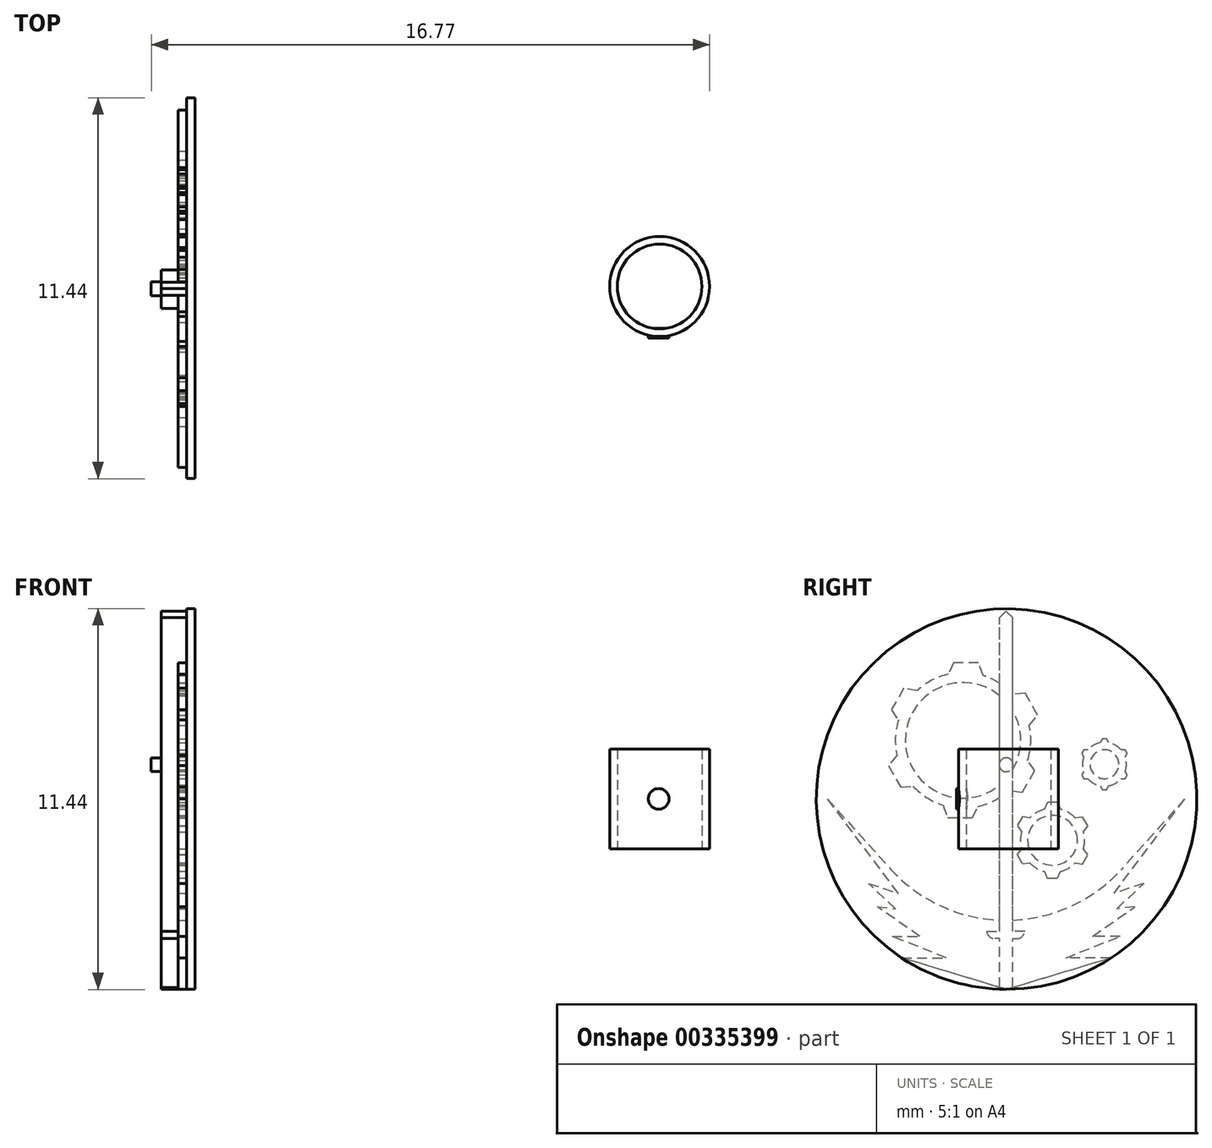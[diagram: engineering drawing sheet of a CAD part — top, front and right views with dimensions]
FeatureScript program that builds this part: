
annotation { "Feature Type Name" : "Feature", "Feature Type Description" : "" }
export const myFeature = defineFeature(function(context is Context, id is Id, definition is map)
    precondition{}
    {
        {
            var Q0;
            Q0=qCreatedBy(makeId("Right.planeOp"),FACE);
            var sketch = newSketch(context, id + "F0", { "sketchPlane" : qUnion([Q0])});
            skCircle(sketch, "E0", {"center": v(0, 0) * mm, "radius": 5.53 * mm});
            skCircle(sketch, "E1", {"center": v(0, 0) * mm, "radius": 5.72 * mm});
            skSolve(sketch);
        }
        {
            var Q0;
            Q0 = qSketchRegion(id + "F0", true);
            var Q1;
            Q1=makeQuery(id+"F0.imprint","IMPRINT",FACE,{"disambiguationData":[TD([[makeQuery(id+"F0.imprint","IMPRINT",EDGE,{"derivedFrom":sQuery(id+"F0.wireOp",EDGE,"E0")}),1.0]])]});
            extrude(context, id + "F1", {"entities" : qUnion([Q0, Q1]), "depth" : 0.25 * mm});
        }
        {
            var Q0;
            Q0=makeQuery(id+"F1.opExtrude","CAP_FACE",FACE,{"disambiguationData":[OSD([sQuery(id+"F0.wireOp",EDGE,"E1")])],"isStart":true});
            var sketch = newSketch(context, id + "F2", { "sketchPlane" : qUnion([Q0])});
            skLineSegment(sketch, "E2", {"start": v(-0.18, -6.05) * mm, "end": v(0.2, -6.05) * mm});
            skLineSegment(sketch, "E3", {"start": v(0.2, -6.05) * mm, "end": v(0.2, -4.2) * mm});
            skLineSegment(sketch, "E4", {"start": v(-0.18, -6.05) * mm, "end": v(-0.18, -4.2) * mm});
            skLineSegment(sketch, "E5", {"start": v(-0.18, -4.2) * mm, "end": v(-0.55, -4.2) * mm});
            skLineSegment(sketch, "E6", {"start": v(-0.55, -4.2) * mm, "end": v(-0.55, -3.97) * mm});
            skLineSegment(sketch, "E7", {"start": v(0.2, -4.2) * mm, "end": v(0.6, -4.2) * mm});
            skLineSegment(sketch, "E8", {"start": v(0.6, -4.2) * mm, "end": v(0.6, -3.97) * mm});
            skLineSegment(sketch, "E9", {"start": v(0.6, -3.97) * mm, "end": v(0.2, -3.97) * mm});
            skLineSegment(sketch, "E10", {"start": v(-0.55, -3.97) * mm, "end": v(-0.18, -3.97) * mm});
            skLineSegment(sketch, "E11", {"start": v(-0.18, -3.97) * mm, "end": v(-0.18, 6.04) * mm});
            skLineSegment(sketch, "E12", {"start": v(0.2, -3.97) * mm, "end": v(0.2, 6.04) * mm});
            skLineSegment(sketch, "E13", {"start": v(-0.18, 6.04) * mm, "end": v(0.2, 6.04) * mm});
            skCircle(sketch, "E14", {"center": v(-1.38, -1.24) * mm, "radius": 0.96 * mm});
            skCircle(sketch, "E15", {"center": v(-1.38, -1.24) * mm, "radius": 0.75 * mm});
            skCircle(sketch, "E16", {"center": v(-2.94, 1.05) * mm, "radius": 0.66 * mm});
            skCircle(sketch, "E17", {"center": v(-2.94, 1.05) * mm, "radius": 0.43 * mm});
            skCircle(sketch, "E18", {"center": v(1.3, 1.76) * mm, "radius": 2.04 * mm});
            skCircle(sketch, "E19", {"center": v(1.3, 1.76) * mm, "radius": 1.73 * mm});
            skLineSegment(sketch, "E20", {"start": v(0.2, 1.03) * mm, "end": v(-0.18, 1.03) * mm, "construction": true});
            skCircle(sketch, "E21", {"center": v(0.01, 1.03) * mm, "radius": 4.67 * mm});
            skLineSegment(sketch, "E22", {"start": v(0.01, -5.71) * mm, "end": v(3.15, -4.77) * mm});
            skPoint(sketch, "E22.startSnap0", {"position": v(0.01, -6.05) * mm});
            skLineSegment(sketch, "E23", {"start": v(3.15, -4.77) * mm, "end": v(1.8, -4.77) * mm});
            skLineSegment(sketch, "E24", {"start": v(1.8, -4.77) * mm, "end": v(3.44, -4.12) * mm});
            skLineSegment(sketch, "E25", {"start": v(3.44, -4.12) * mm, "end": v(2.6, -4.12) * mm});
            skLineSegment(sketch, "E26", {"start": v(2.6, -4.12) * mm, "end": v(3.88, -3.23) * mm});
            skLineSegment(sketch, "E27", {"start": v(3.88, -3.23) * mm, "end": v(3.34, -3.3) * mm});
            skLineSegment(sketch, "E28", {"start": v(3.34, -3.3) * mm, "end": v(4.15, -2.54) * mm});
            skLineSegment(sketch, "E29", {"start": v(4.15, -2.54) * mm, "end": v(3.25, -2.83) * mm});
            skLineSegment(sketch, "E30", {"start": v(3.25, -2.83) * mm, "end": v(5.38, 0) * mm});
            skLineSegment(sketch, "E31", {"start": v(5.38, 0) * mm, "end": v(2.83, -2.83) * mm});
            skLineSegment(sketch, "E32", {"start": v(0.01, 6.04) * mm, "end": v(0.01, -6.05) * mm, "construction": true});
            skLineSegment(sketch, "E33.MirrorCS", {"start": v(0.01, -5.71) * mm, "end": v(-3.12, -4.77) * mm});
            skLineSegment(sketch, "E34.MirrorCS", {"start": v(-3.12, -4.77) * mm, "end": v(-1.78, -4.77) * mm});
            skLineSegment(sketch, "E35.MirrorCS", {"start": v(-1.78, -4.77) * mm, "end": v(-3.41, -4.12) * mm});
            skLineSegment(sketch, "E36.MirrorCS", {"start": v(-3.41, -4.12) * mm, "end": v(-2.58, -4.12) * mm});
            skLineSegment(sketch, "E37.MirrorCS", {"start": v(-2.58, -4.12) * mm, "end": v(-3.86, -3.23) * mm});
            skLineSegment(sketch, "E38.MirrorCS", {"start": v(-3.86, -3.23) * mm, "end": v(-3.31, -3.3) * mm});
            skLineSegment(sketch, "E39.MirrorCS", {"start": v(-3.31, -3.3) * mm, "end": v(-4.12, -2.54) * mm});
            skLineSegment(sketch, "E40.MirrorCS", {"start": v(-4.12, -2.54) * mm, "end": v(-3.23, -2.83) * mm});
            skLineSegment(sketch, "E41.MirrorCS", {"start": v(-3.23, -2.83) * mm, "end": v(-5.35, 0) * mm});
            skLineSegment(sketch, "E42.MirrorCS", {"start": v(-5.35, 0) * mm, "end": v(-2.8, -2.83) * mm});
            skLineSegment(sketch, "E43", {"start": v(-3.07, 1.7) * mm, "end": v(-3, 1.8) * mm});
            skLineSegment(sketch, "E44", {"start": v(-3, 1.8) * mm, "end": v(-2.88, 1.8) * mm});
            skLineSegment(sketch, "E45", {"start": v(-2.88, 1.8) * mm, "end": v(-2.81, 1.7) * mm});
            skLineSegment(sketch, "E46.1.0", {"start": v(-3.56, 1.48) * mm, "end": v(-3.44, 1.48) * mm});
            skLineSegment(sketch, "E46.1.1", {"start": v(-3.63, 1.37) * mm, "end": v(-3.56, 1.48) * mm});
            skLineSegment(sketch, "E46.1.2", {"start": v(-3.56, 1.26) * mm, "end": v(-3.63, 1.37) * mm});
            skLineSegment(sketch, "E46.2.0", {"start": v(-3.63, 0.72) * mm, "end": v(-3.56, 0.83) * mm});
            skLineSegment(sketch, "E46.2.1", {"start": v(-3.56, 0.61) * mm, "end": v(-3.63, 0.72) * mm});
            skLineSegment(sketch, "E46.2.2", {"start": v(-3.44, 0.61) * mm, "end": v(-3.56, 0.61) * mm});
            skLineSegment(sketch, "E46.3.0", {"start": v(-3, 0.29) * mm, "end": v(-3.07, 0.4) * mm});
            skLineSegment(sketch, "E46.3.1", {"start": v(-2.88, 0.29) * mm, "end": v(-3, 0.29) * mm});
            skLineSegment(sketch, "E46.3.2", {"start": v(-2.81, 0.4) * mm, "end": v(-2.88, 0.29) * mm});
            skLineSegment(sketch, "E46.4.0", {"start": v(-2.32, 0.61) * mm, "end": v(-2.44, 0.61) * mm});
            skLineSegment(sketch, "E46.4.1", {"start": v(-2.25, 0.72) * mm, "end": v(-2.32, 0.61) * mm});
            skLineSegment(sketch, "E46.4.2", {"start": v(-2.32, 0.83) * mm, "end": v(-2.25, 0.72) * mm});
            skLineSegment(sketch, "E46.5.0", {"start": v(-2.25, 1.37) * mm, "end": v(-2.32, 1.26) * mm});
            skLineSegment(sketch, "E46.5.1", {"start": v(-2.32, 1.48) * mm, "end": v(-2.25, 1.37) * mm});
            skLineSegment(sketch, "E46.5.2", {"start": v(-2.44, 1.48) * mm, "end": v(-2.32, 1.48) * mm});
            skLineSegment(sketch, "E47", {"start": v(-1.62, -0.3) * mm, "end": v(-1.54, -0.1) * mm});
            skLineSegment(sketch, "E48", {"start": v(-1.54, -0.1) * mm, "end": v(-1.23, -0.1) * mm});
            skLineSegment(sketch, "E49", {"start": v(-1.23, -0.1) * mm, "end": v(-1.14, -0.3) * mm});
            skLineSegment(sketch, "E50.1.0", {"start": v(-2.3, -0.98) * mm, "end": v(-2.45, -0.81) * mm});
            skLineSegment(sketch, "E50.1.1", {"start": v(-2.45, -0.81) * mm, "end": v(-2.29, -0.54) * mm});
            skLineSegment(sketch, "E50.1.2", {"start": v(-2.29, -0.54) * mm, "end": v(-2.06, -0.56) * mm});
            skLineSegment(sketch, "E50.2.0", {"start": v(-2.06, -1.92) * mm, "end": v(-2.28, -1.95) * mm});
            skLineSegment(sketch, "E50.2.1", {"start": v(-2.28, -1.95) * mm, "end": v(-2.44, -1.68) * mm});
            skLineSegment(sketch, "E50.2.2", {"start": v(-2.44, -1.68) * mm, "end": v(-2.3, -1.5) * mm});
            skLineSegment(sketch, "E50.3.0", {"start": v(-1.14, -2.17) * mm, "end": v(-1.22, -2.38) * mm});
            skLineSegment(sketch, "E50.3.1", {"start": v(-1.22, -2.38) * mm, "end": v(-1.53, -2.38) * mm});
            skLineSegment(sketch, "E50.3.2", {"start": v(-1.53, -2.38) * mm, "end": v(-1.62, -2.17) * mm});
            skLineSegment(sketch, "E50.4.0", {"start": v(-0.45, -1.5) * mm, "end": v(-0.31, -1.67) * mm});
            skLineSegment(sketch, "E50.4.1", {"start": v(-0.31, -1.67) * mm, "end": v(-0.47, -1.94) * mm});
            skLineSegment(sketch, "E50.4.2", {"start": v(-0.47, -1.94) * mm, "end": v(-0.7, -1.92) * mm});
            skLineSegment(sketch, "E50.5.0", {"start": v(-0.7, -0.56) * mm, "end": v(-0.48, -0.53) * mm});
            skLineSegment(sketch, "E50.5.1", {"start": v(-0.48, -0.53) * mm, "end": v(-0.32, -0.8) * mm});
            skLineSegment(sketch, "E50.5.2", {"start": v(-0.32, -0.8) * mm, "end": v(-0.45, -0.98) * mm});
            skLineSegment(sketch, "E51", {"start": v(0.7, 3.7) * mm, "end": v(0.84, 4.09) * mm});
            skLineSegment(sketch, "E52", {"start": v(0.84, 4.09) * mm, "end": v(1.6, 4.09) * mm});
            skLineSegment(sketch, "E53", {"start": v(1.6, 4.09) * mm, "end": v(1.75, 3.75) * mm});
            skLineSegment(sketch, "E54.1.0", {"start": v(-0.68, 2.21) * mm, "end": v(-0.94, 2.52) * mm});
            skLineSegment(sketch, "E54.1.1", {"start": v(-0.94, 2.52) * mm, "end": v(-0.56, 3.17) * mm});
            skLineSegment(sketch, "E54.1.2", {"start": v(-0.56, 3.17) * mm, "end": v(-0.2, 3.14) * mm});
            skLineSegment(sketch, "E54.2.0", {"start": v(-0.07, 0.27) * mm, "end": v(-0.47, 0.2) * mm});
            skLineSegment(sketch, "E54.2.1", {"start": v(-0.47, 0.2) * mm, "end": v(-0.85, 0.85) * mm});
            skLineSegment(sketch, "E54.2.2", {"start": v(-0.85, 0.85) * mm, "end": v(-0.64, 1.15) * mm});
            skLineSegment(sketch, "E54.3.0", {"start": v(1.91, -0.18) * mm, "end": v(1.77, -0.56) * mm});
            skLineSegment(sketch, "E54.3.1", {"start": v(1.77, -0.56) * mm, "end": v(1.02, -0.56) * mm});
            skLineSegment(sketch, "E54.3.2", {"start": v(1.02, -0.56) * mm, "end": v(0.86, -0.22) * mm});
            skLineSegment(sketch, "E54.4.0", {"start": v(3.3, 1.31) * mm, "end": v(3.55, 1) * mm});
            skLineSegment(sketch, "E54.4.1", {"start": v(3.55, 1) * mm, "end": v(3.18, 0.35) * mm});
            skLineSegment(sketch, "E54.4.2", {"start": v(3.18, 0.35) * mm, "end": v(2.8, 0.39) * mm});
            skLineSegment(sketch, "E54.5.0", {"start": v(2.69, 3.26) * mm, "end": v(3.09, 3.33) * mm});
            skLineSegment(sketch, "E54.5.1", {"start": v(3.09, 3.33) * mm, "end": v(3.46, 2.68) * mm});
            skLineSegment(sketch, "E54.5.2", {"start": v(3.46, 2.68) * mm, "end": v(3.25, 2.37) * mm});
            skSolve(sketch);
        }
        {
            var Q0;
            {var subQ0=sQuery(id+"F2.wireOp",EDGE,"E5");Q0=makeQuery(id+"F2.imprint","IMPRINT",FACE,{"disambiguationData":[TD([[makeQuery(id+"F2.imprint","IMPRINT",EDGE,{"derivedFrom":subQ0}),1.0]])]});}
            var Q1;
            {var subQ9=sQuery(id+"F2.wireOp",EDGE,"E7");Q1=makeQuery(id+"F2.imprint","IMPRINT",FACE,{"disambiguationData":[TD([[makeQuery(id+"F2.imprint","IMPRINT",EDGE,{"derivedFrom":subQ9}),-1.0]])]});}
            extrude(context, id + "F3", {"entities" : qUnion([Q0, Q1]), "operationType" : NewBodyOperationType.ADD, "depth" : 0.25 * mm});
        }
        {
            var Q0;
            {var subQ0=sQuery(id+"F2.wireOp",EDGE,"E21");var subQ1=sQuery(id+"F2.wireOp",EDGE,"E11");var subQ2=makeQuery(id+"F2.imprint","INTERSECT",VERTEX,{"disambiguationData":[OD(0.0)],"derivedFrom":[subQ1,subQ0]});Q0=makeQuery(id+"F2.imprint","IMPRINT",FACE,{"disambiguationData":[TD([[makeQuery(id+"F2.imprint","IMPRINT",EDGE,{"disambiguationData":[TD([[subQ2,-1.0]])],"derivedFrom":subQ1}),-1.0]])]});}
            var Q1;
            {var subQ11=sQuery(id+"F2.wireOp",EDGE,"E5");Q1=makeQuery(id+"F2.imprint","IMPRINT",FACE,{"disambiguationData":[TD([[makeQuery(id+"F2.imprint","IMPRINT",EDGE,{"derivedFrom":subQ11}),-1.0]])]});}
            var Q2;
            {var subQ0=sQuery(id+"F2.wireOp",EDGE,"E18");var subQ6=sQuery(id+"F2.wireOp",EDGE,"E11");var subQ7=makeQuery(id+"F2.imprint","INTERSECT",VERTEX,{"disambiguationData":[OD(0.0)],"derivedFrom":[subQ6,subQ0]});Q2=makeQuery(id+"F2.imprint","IMPRINT",FACE,{"disambiguationData":[TD([[makeQuery(id+"F2.imprint","IMPRINT",EDGE,{"disambiguationData":[TD([[subQ7,-1.0]])],"derivedFrom":subQ6}),-1.0]])]});}
            var Q3;
            {var subQ0=sQuery(id+"F2.wireOp",EDGE,"E18");var subQ1=sQuery(id+"F2.wireOp",EDGE,"E11");var subQ2=makeQuery(id+"F2.imprint","INTERSECT",VERTEX,{"disambiguationData":[OD(1.0)],"derivedFrom":[subQ1,subQ0]});Q3=makeQuery(id+"F2.imprint","IMPRINT",FACE,{"disambiguationData":[TD([[makeQuery(id+"F2.imprint","IMPRINT",EDGE,{"disambiguationData":[TD([[subQ2,-1.0]])],"derivedFrom":subQ1}),-1.0]])]});}
            var Q4;
            {var subQ0=sQuery(id+"F2.wireOp",EDGE,"E19");var subQ1=sQuery(id+"F2.wireOp",EDGE,"E11");var subQ2=makeQuery(id+"F2.imprint","INTERSECT",VERTEX,{"disambiguationData":[OD(1.0)],"derivedFrom":[subQ1,subQ0]});Q4=makeQuery(id+"F2.imprint","IMPRINT",FACE,{"disambiguationData":[TD([[makeQuery(id+"F2.imprint","IMPRINT",EDGE,{"disambiguationData":[TD([[subQ2,-1.0]])],"derivedFrom":subQ1}),-1.0]])]});}
            var Q5;
            {var subQ0=sQuery(id+"F2.wireOp",EDGE,"E19");var subQ1=sQuery(id+"F2.wireOp",EDGE,"E11");var subQ2=makeQuery(id+"F2.imprint","INTERSECT",VERTEX,{"disambiguationData":[OD(0.0)],"derivedFrom":[subQ1,subQ0]});Q5=makeQuery(id+"F2.imprint","IMPRINT",FACE,{"disambiguationData":[TD([[makeQuery(id+"F2.imprint","IMPRINT",EDGE,{"disambiguationData":[TD([[subQ2,-1.0]])],"derivedFrom":subQ1}),-1.0]])]});}
            var Q6;
            {var subQ0=sQuery(id+"F2.wireOp",EDGE,"E54.2.0");var subQ1=sQuery(id+"F2.wireOp",EDGE,"E11");var subQ2=makeQuery(id+"F2.imprint","INTERSECT",VERTEX,{"derivedFrom":[subQ1,subQ0]});Q6=makeQuery(id+"F2.imprint","IMPRINT",FACE,{"disambiguationData":[TD([[makeQuery(id+"F2.imprint","IMPRINT",EDGE,{"disambiguationData":[TD([[subQ2,-1.0]])],"derivedFrom":subQ1}),-1.0]])]});}
            extrude(context, id + "F4", {"entities" : qUnion([Q0, Q1, Q2, Q3, Q4, Q5, Q6]), "operationType" : NewBodyOperationType.ADD, "depth" : 0.76 * mm});
        }
        {
            var Q0;
            {var subQ0=sQuery(id+"F2.wireOp",EDGE,"E46.2.0");Q0=makeQuery(id+"F2.imprint","IMPRINT",FACE,{"disambiguationData":[TD([[makeQuery(id+"F2.imprint","IMPRINT",EDGE,{"derivedFrom":subQ0}),-1.0]])]});}
            var Q1;
            {var subQ0=sQuery(id+"F2.wireOp",EDGE,"E46.1.0");Q1=makeQuery(id+"F2.imprint","IMPRINT",FACE,{"disambiguationData":[TD([[makeQuery(id+"F2.imprint","IMPRINT",EDGE,{"derivedFrom":subQ0}),-1.0]])]});}
            var Q2;
            {var subQ0=sQuery(id+"F2.wireOp",EDGE,"E43");Q2=makeQuery(id+"F2.imprint","IMPRINT",FACE,{"disambiguationData":[TD([[makeQuery(id+"F2.imprint","IMPRINT",EDGE,{"derivedFrom":subQ0}),-1.0]])]});}
            var Q3;
            {var subQ0=sQuery(id+"F2.wireOp",EDGE,"E46.5.0");Q3=makeQuery(id+"F2.imprint","IMPRINT",FACE,{"disambiguationData":[TD([[makeQuery(id+"F2.imprint","IMPRINT",EDGE,{"derivedFrom":subQ0}),-1.0]])]});}
            var Q4;
            {var subQ0=sQuery(id+"F2.wireOp",EDGE,"E46.4.0");Q4=makeQuery(id+"F2.imprint","IMPRINT",FACE,{"disambiguationData":[TD([[makeQuery(id+"F2.imprint","IMPRINT",EDGE,{"derivedFrom":subQ0}),-1.0]])]});}
            var Q5;
            {var subQ0=sQuery(id+"F2.wireOp",EDGE,"E46.3.0");Q5=makeQuery(id+"F2.imprint","IMPRINT",FACE,{"disambiguationData":[TD([[makeQuery(id+"F2.imprint","IMPRINT",EDGE,{"derivedFrom":subQ0}),-1.0]])]});}
            var Q6;
            Q6=makeQuery(id+"F2.imprint","IMPRINT",FACE,{"disambiguationData":[TD([[makeQuery(id+"F2.imprint","IMPRINT",EDGE,{"derivedFrom":sQuery(id+"F2.wireOp",EDGE,"E17")}),-1.0]])]});
            var Q7;
            {var subQ0=sQuery(id+"F2.wireOp",EDGE,"E50.2.0");Q7=makeQuery(id+"F2.imprint","IMPRINT",FACE,{"disambiguationData":[TD([[makeQuery(id+"F2.imprint","IMPRINT",EDGE,{"derivedFrom":subQ0}),-1.0]])]});}
            var Q8;
            {var subQ0=sQuery(id+"F2.wireOp",EDGE,"E50.1.0");Q8=makeQuery(id+"F2.imprint","IMPRINT",FACE,{"disambiguationData":[TD([[makeQuery(id+"F2.imprint","IMPRINT",EDGE,{"derivedFrom":subQ0}),-1.0]])]});}
            var Q9;
            {var subQ0=sQuery(id+"F2.wireOp",EDGE,"E47");Q9=makeQuery(id+"F2.imprint","IMPRINT",FACE,{"disambiguationData":[TD([[makeQuery(id+"F2.imprint","IMPRINT",EDGE,{"derivedFrom":subQ0}),-1.0]])]});}
            var Q10;
            {var subQ0=sQuery(id+"F2.wireOp",EDGE,"E50.5.0");Q10=makeQuery(id+"F2.imprint","IMPRINT",FACE,{"disambiguationData":[TD([[makeQuery(id+"F2.imprint","IMPRINT",EDGE,{"derivedFrom":subQ0}),-1.0]])]});}
            var Q11;
            {var subQ0=sQuery(id+"F2.wireOp",EDGE,"E50.4.0");Q11=makeQuery(id+"F2.imprint","IMPRINT",FACE,{"disambiguationData":[TD([[makeQuery(id+"F2.imprint","IMPRINT",EDGE,{"derivedFrom":subQ0}),-1.0]])]});}
            var Q12;
            {var subQ0=sQuery(id+"F2.wireOp",EDGE,"E50.3.0");Q12=makeQuery(id+"F2.imprint","IMPRINT",FACE,{"disambiguationData":[TD([[makeQuery(id+"F2.imprint","IMPRINT",EDGE,{"derivedFrom":subQ0}),-1.0]])]});}
            var Q13;
            Q13=makeQuery(id+"F2.imprint","IMPRINT",FACE,{"disambiguationData":[TD([[makeQuery(id+"F2.imprint","IMPRINT",EDGE,{"derivedFrom":sQuery(id+"F2.wireOp",EDGE,"E15")}),-1.0]])]});
            var Q14;
            {var subQ0=sQuery(id+"F2.wireOp",EDGE,"E18");var subQ2=sQuery(id+"F2.wireOp",EDGE,"E11");var subQ8=makeQuery(id+"F2.imprint","INTERSECT",VERTEX,{"disambiguationData":[OD(0.0)],"derivedFrom":[subQ2,subQ0]});Q14=makeQuery(id+"F2.imprint","IMPRINT",FACE,{"disambiguationData":[TD([[makeQuery(id+"F2.imprint","IMPRINT",EDGE,{"disambiguationData":[TD([[subQ8,-1.0]])],"derivedFrom":subQ2}),1.0]])]});}
            var Q15;
            {var subQ0=sQuery(id+"F2.wireOp",EDGE,"E54.2.1");Q15=makeQuery(id+"F2.imprint","IMPRINT",FACE,{"disambiguationData":[TD([[makeQuery(id+"F2.imprint","IMPRINT",EDGE,{"derivedFrom":subQ0}),-1.0]])]});}
            var Q16;
            {var subQ0=sQuery(id+"F2.wireOp",EDGE,"E54.3.0");Q16=makeQuery(id+"F2.imprint","IMPRINT",FACE,{"disambiguationData":[TD([[makeQuery(id+"F2.imprint","IMPRINT",EDGE,{"derivedFrom":subQ0}),-1.0]])]});}
            var Q17;
            {var subQ0=sQuery(id+"F2.wireOp",EDGE,"E54.4.0");Q17=makeQuery(id+"F2.imprint","IMPRINT",FACE,{"disambiguationData":[TD([[makeQuery(id+"F2.imprint","IMPRINT",EDGE,{"derivedFrom":subQ0}),-1.0]])]});}
            var Q18;
            {var subQ0=sQuery(id+"F2.wireOp",EDGE,"E54.5.0");Q18=makeQuery(id+"F2.imprint","IMPRINT",FACE,{"disambiguationData":[TD([[makeQuery(id+"F2.imprint","IMPRINT",EDGE,{"derivedFrom":subQ0}),-1.0]])]});}
            var Q19;
            {var subQ0=sQuery(id+"F2.wireOp",EDGE,"E51");Q19=makeQuery(id+"F2.imprint","IMPRINT",FACE,{"disambiguationData":[TD([[makeQuery(id+"F2.imprint","IMPRINT",EDGE,{"derivedFrom":subQ0}),-1.0]])]});}
            var Q20;
            {var subQ0=sQuery(id+"F2.wireOp",EDGE,"E54.1.0");Q20=makeQuery(id+"F2.imprint","IMPRINT",FACE,{"disambiguationData":[TD([[makeQuery(id+"F2.imprint","IMPRINT",EDGE,{"derivedFrom":subQ0}),-1.0]])]});}
            var Q21;
            {var subQ0=sQuery(id+"F2.wireOp",EDGE,"E18");var subQ4=sQuery(id+"F2.wireOp",EDGE,"E12");var subQ7=makeQuery(id+"F2.imprint","INTERSECT",VERTEX,{"disambiguationData":[OD(0.0)],"derivedFrom":[subQ4,subQ0]});Q21=makeQuery(id+"F2.imprint","IMPRINT",FACE,{"disambiguationData":[TD([[makeQuery(id+"F2.imprint","IMPRINT",EDGE,{"disambiguationData":[TD([[subQ7,-1.0]])],"derivedFrom":subQ4}),-1.0]])]});}
            extrude(context, id + "F5", {"entities" : qUnion([Q0, Q1, Q2, Q3, Q4, Q5, Q6, Q7, Q8, Q9, Q10, Q11, Q12, Q13, Q14, Q15, Q16, Q17, Q18, Q19, Q20, Q21]), "operationType" : NewBodyOperationType.ADD, "depth" : 0.25 * mm});
        }
        {
            var Q0;
            Q0=makeQuery(id+"F4.opExtrude","SWEPT_EDGE",EDGE,{"disambiguationData":[OSD([sQuery(id+"F2.wireOp",EDGE,"E5"),sQuery(id+"F2.wireOp",EDGE,"E6")])]});
            fillet(context, id + "F6", {"entities" : qUnion([Q0]), "radius" : 0.25 * mm, "tangentPropagation" : true, "allowEdgeOverflow" : false});
        }
        {
            var Q0;
            Q0=makeQuery(id+"F4.opExtrude","SWEPT_EDGE",EDGE,{"disambiguationData":[OSD([sQuery(id+"F2.wireOp",EDGE,"E7"),sQuery(id+"F2.wireOp",EDGE,"E8")])]});
            fillet(context, id + "F7", {"entities" : qUnion([Q0]), "radius" : 0.25 * mm, "tangentPropagation" : true, "allowEdgeOverflow" : false});
        }
        {
            var Q0;
            Q0=makeQuery(id+"F4.opExtrude","SWEPT_EDGE",EDGE,{"disambiguationData":[OSD([sQuery(id+"F2.wireOp",EDGE,"E11"),sQuery(id+"F2.wireOp",EDGE,"E21")])]});
            var Q1;
            Q1=makeQuery(id+"F4.opExtrude","SWEPT_EDGE",EDGE,{"disambiguationData":[OSD([sQuery(id+"F2.wireOp",EDGE,"E12"),sQuery(id+"F2.wireOp",EDGE,"E21")])]});
            chamfer(context, id + "F8", {"entities" : qUnion([Q0, Q1]), "width" : 0.25 * mm, "tangentPropagation" : true});
        }
        {
            var Q0;
            Q0=qCreatedBy(makeId("Top.planeOp"),FACE);
            var sketch = newSketch(context, id + "F9", { "sketchPlane" : qUnion([Q0])});
            skCircle(sketch, "E55", {"center": v(14.2, 0.05) * mm, "radius": 1.5 * mm});
            skCircle(sketch, "E56", {"center": v(14.2, 0.05) * mm, "radius": 1.27 * mm});
            skSolve(sketch);
        }
        {
            var Q0;
            Q0 = qSketchRegion(id + "F9", true);
            extrude(context, id + "F10", {"entities" : qUnion([Q0]), "endBound" : BoundingType.SYMMETRIC, "depth" : 3 * mm});
        }
        {
            var Q0;
            Q0=qCreatedBy(makeId("Front.planeOp"),FACE);
            var sketch = newSketch(context, id + "F11", { "sketchPlane" : qUnion([Q0])});
            skCircle(sketch, "E57", {"center": v(14.18, 0) * mm, "radius": 0.3 * mm});
            skSolve(sketch);
        }
        {
            var Q0;
            Q0 = qSketchRegion(id + "F11", true);
            extrude(context, id + "F12", {"entities" : qUnion([Q0]), "operationType" : NewBodyOperationType.ADD, "depth" : 1.5 * mm});
        }
        {
            var Q0;
            Q0=makeQuery(id+"F12.opExtrude","CAP_FACE",FACE,{"disambiguationData":[OSD([sQuery(id+"F11.wireOp",EDGE,"E57")])],"isStart":true});
            var sketch = newSketch(context, id + "F13", { "sketchPlane" : qUnion([Q0])});
            skCircle(sketch, "E58.0", {"center": v(-14.18, 0) * mm, "radius": 0.3 * mm});
            skSolve(sketch);
        }
        {
            var Q0;
            Q0 = qSketchRegion(id + "F13", true);
            extrude(context, id + "F14", {"entities" : qUnion([Q0]), "operationType" : NewBodyOperationType.REMOVE, "oppositeDirection" : true, "depth" : 1.2 * mm});
        }
        {
            var Q0;
            Q0=makeQuery(id+"F4.opExtrude","CAP_FACE",FACE,{"disambiguationData":[OSD([sQuery(id+"F2.wireOp",EDGE,"E3"),sQuery(id+"F2.wireOp",EDGE,"E4"),sQuery(id+"F2.wireOp",EDGE,"E5"),sQuery(id+"F2.wireOp",EDGE,"E6"),sQuery(id+"F2.wireOp",EDGE,"E7"),sQuery(id+"F2.wireOp",EDGE,"E8"),sQuery(id+"F2.wireOp",EDGE,"E9"),sQuery(id+"F2.wireOp",EDGE,"E10"),sQuery(id+"F2.wireOp",EDGE,"E11"),sQuery(id+"F2.wireOp",EDGE,"E12"),sQuery(id+"F2.wireOp",EDGE,"E21"),sQuery(id+"F2.wireOp",EDGE,"E22"),sQuery(id+"F2.wireOp",EDGE,"E33.MirrorCS")])],"isStart":false});
            var sketch = newSketch(context, id + "F15", { "sketchPlane" : qUnion([Q0])});
            skLineSegment(sketch, "E59.0", {"start": v(0.01, 6.04) * mm, "end": v(0.01, -6.05) * mm});
            skPoint(sketch, "E60.0", {"position": v(0.01, 1.03) * mm});
            skCircle(sketch, "E61", {"center": v(0.01, 1.03) * mm, "radius": 0.2 * mm});
            skSolve(sketch);
        }
        {
            var Q0;
            Q0 = qSketchRegion(id + "F15", true);
            extrude(context, id + "F16", {"entities" : qUnion([Q0]), "operationType" : NewBodyOperationType.ADD, "depth" : .3 * mm});
        }
    });
